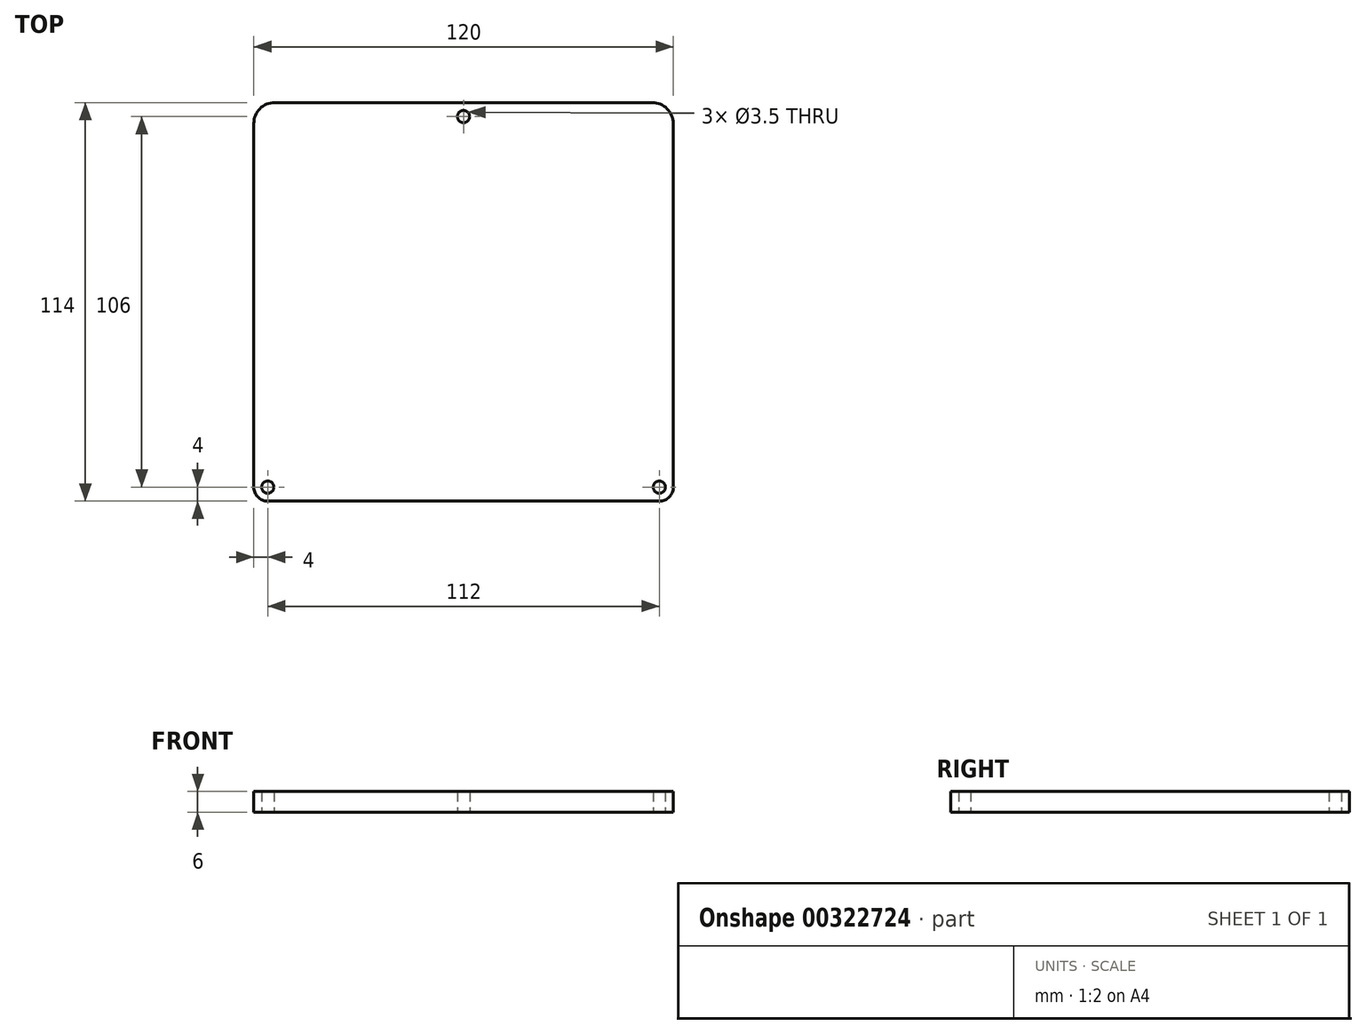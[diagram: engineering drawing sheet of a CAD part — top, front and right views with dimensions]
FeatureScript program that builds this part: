
annotation { "Feature Type Name" : "Feature", "Feature Type Description" : "" }
export const myFeature = defineFeature(function(context is Context, id is Id, definition is map)
    precondition{}
    {
        {
            var Q0;
            Q0=qCreatedBy(makeId("Top.planeOp"),FACE);
            var sketch = newSketch(context, id + "F0", { "sketchPlane" : qUnion([Q0])});
            skLineSegment(sketch, "E0.bottom", {"start": v(-60, 60) * mm, "end": v(60, 60) * mm});
            skLineSegment(sketch, "E0.top", {"start": v(-60, -54) * mm, "end": v(60, -54) * mm});
            skLineSegment(sketch, "E0.left", {"start": v(-60, 60) * mm, "end": v(-60, -54) * mm});
            skLineSegment(sketch, "E0.right", {"start": v(60, 60) * mm, "end": v(60, -54) * mm});
            skCircle(sketch, "E1", {"center": v(-56, -50) * mm, "radius": 1.75 * mm});
            skCircle(sketch, "E2.MirrorC", {"center": v(56, -50) * mm, "radius": 1.75 * mm});
            skCircle(sketch, "E3", {"center": v(0, 56) * mm, "radius": 1.75 * mm});
            skSolve(sketch);
        }
        {
            var Q0;
            Q0=makeQuery(id+"F0.imprint","IMPRINT",FACE,{"disambiguationData":[TD([[makeQuery(id+"F0.imprint","IMPRINT",EDGE,{"derivedFrom":sQuery(id+"F0.wireOp",EDGE,"E0.bottom")}),-1.0]])]});
            extrude(context, id + "F1", {"entities" : qUnion([Q0]), "depth" : 6 * mm});
        }
        {
            var Q0;
            Q0=makeQuery(id+"F1.opExtrude","SWEPT_EDGE",EDGE,{"disambiguationData":[OSD([sQuery(id+"F0.wireOp",EDGE,"E0.bottom"),sQuery(id+"F0.wireOp",EDGE,"E0.left")])]});
            var Q1;
            Q1=makeQuery(id+"F1.opExtrude","SWEPT_EDGE",EDGE,{"disambiguationData":[OSD([sQuery(id+"F0.wireOp",EDGE,"E0.bottom"),sQuery(id+"F0.wireOp",EDGE,"E0.right")])]});
            fillet(context, id + "F2", {"entities" : qUnion([Q0, Q1]), "tangentPropagation" : true, "radius" : 6 * mm, "defaultsChanged" : false, "vertexSettings" : [], "allowEdgeOverflow" : false});
        }
        {
            var Q0;
            Q0=makeQuery(id+"F1.opExtrude","SWEPT_EDGE",EDGE,{"disambiguationData":[OSD([sQuery(id+"F0.wireOp",EDGE,"E0.top"),sQuery(id+"F0.wireOp",EDGE,"E0.left")])]});
            var Q1;
            Q1=makeQuery(id+"F1.opExtrude","SWEPT_EDGE",EDGE,{"disambiguationData":[OSD([sQuery(id+"F0.wireOp",EDGE,"E0.top"),sQuery(id+"F0.wireOp",EDGE,"E0.right")])]});
            fillet(context, id + "F3", {"entities" : qUnion([Q0, Q1]), "tangentPropagation" : true, "radius" : 4 * mm, "defaultsChanged" : false, "vertexSettings" : [], "allowEdgeOverflow" : false});
        }
    });
